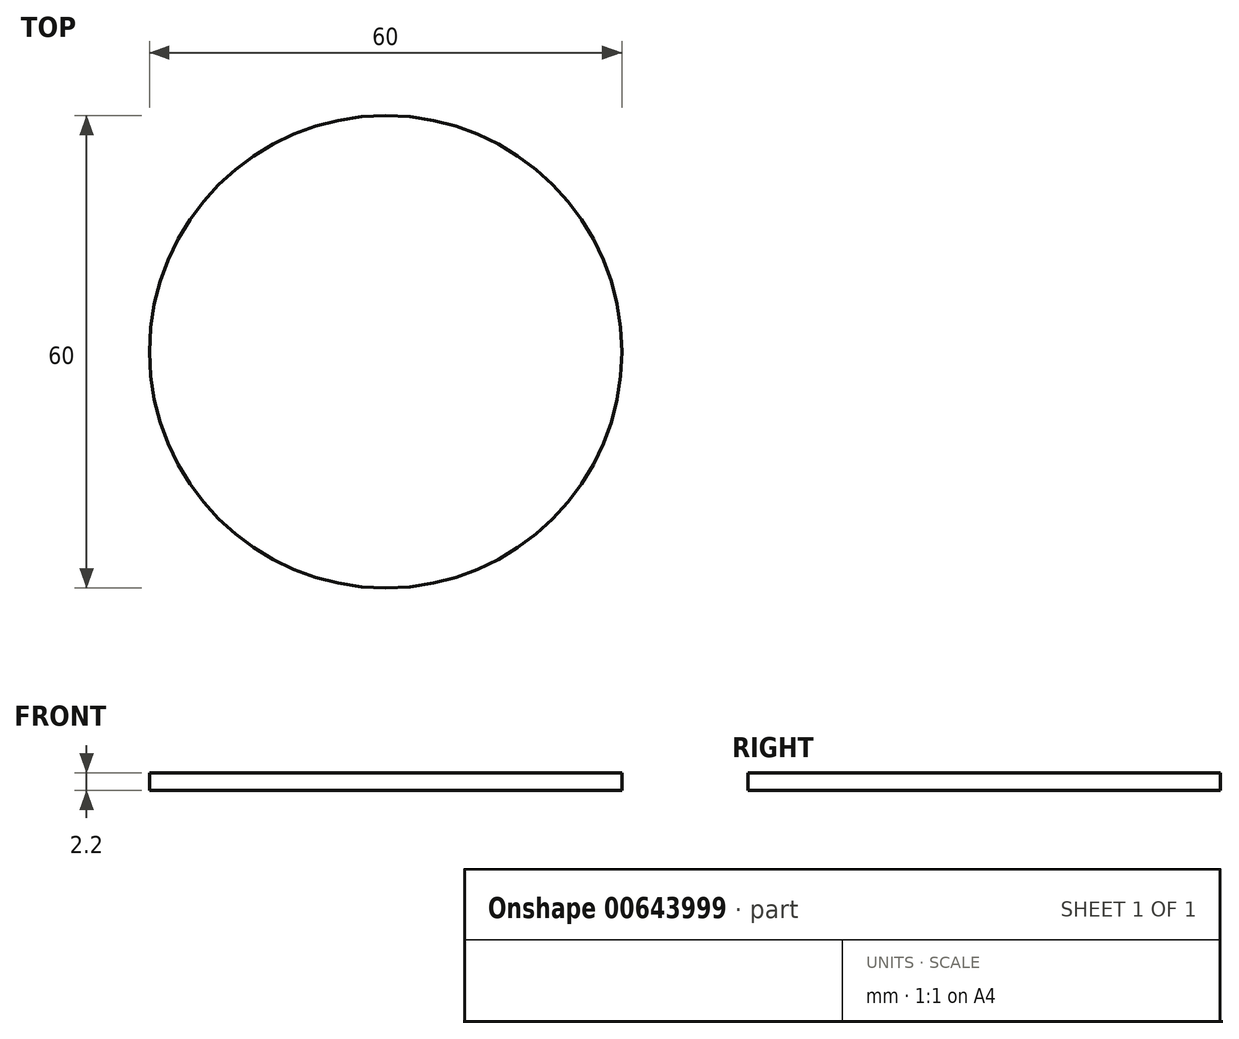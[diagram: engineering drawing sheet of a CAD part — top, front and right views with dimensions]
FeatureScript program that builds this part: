
annotation { "Feature Type Name" : "Feature", "Feature Type Description" : "" }
export const myFeature = defineFeature(function(context is Context, id is Id, definition is map)
    precondition{}
    {
        {
            var Q0;
            Q0=qCreatedBy(makeId("Top.planeOp"),FACE);
            var sketch = newSketch(context, id + "F0", { "sketchPlane" : qUnion([Q0])});
            skCircle(sketch, "E0", {"center": v(0, 0) * mm, "radius": 30 * mm});
            skSolve(sketch);
        }
        {
            var Q0;
            Q0=makeQuery(id+"F0.imprint","IMPRINT",FACE,{"disambiguationData":[TD([[makeQuery(id+"F0.imprint","IMPRINT",EDGE,{"derivedFrom":sQuery(id+"F0.wireOp",EDGE,"E0")}),1.0]])]});
            extrude(context, id + "F1", {"entities" : qUnion([Q0]), "depth" : 2.2 * mm, "offsetDistance" : 25 * mm});
        }
    });
